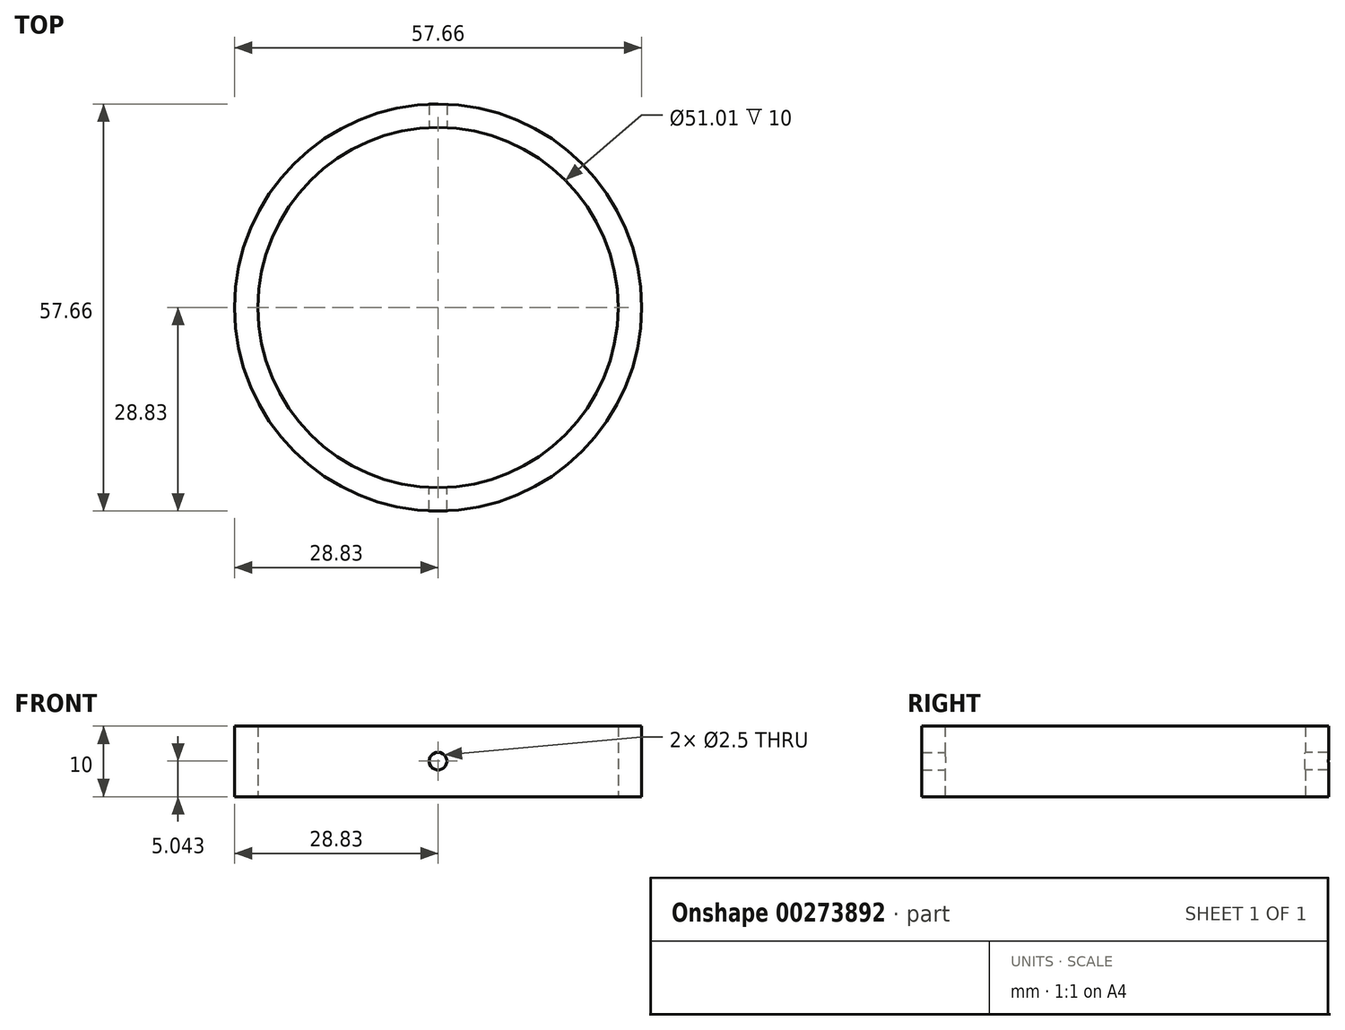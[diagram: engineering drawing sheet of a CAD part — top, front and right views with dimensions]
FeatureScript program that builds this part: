
annotation { "Feature Type Name" : "Feature", "Feature Type Description" : "" }
export const myFeature = defineFeature(function(context is Context, id is Id, definition is map)
    precondition{}
    {
        {
            var Q0;
            Q0=qCreatedBy(makeId("Top.planeOp"),FACE);
            var sketch = newSketch(context, id + "F0", { "sketchPlane" : qUnion([Q0])});
            skCircle(sketch, "E0", {"center": v(0, -0.27) * mm, "radius": 28.67 * mm});
            skSolve(sketch);
        }
        {
            var Q0;
            Q0=qCreatedBy(makeId("Top.planeOp"),FACE);
            cPlane(context, id + "F1", {"entities" : qUnion([Q0]), "cplaneType" : CPlaneType.OFFSET, "offset" : 140 * mm, "width" : 150 * mm, "height" : 150 * mm});
        }
        {
            var Q0;
            Q0=qCreatedBy(id+"F1.planeOp",FACE);
            var sketch = newSketch(context, id + "F2", { "sketchPlane" : qUnion([Q0])});
            skCircle(sketch, "E1", {"center": v(0, 0.28) * mm, "radius": 45.83 * mm});
            skSolve(sketch);
        }
        {
            var Q0;
            Q0=makeQuery(id+"F2.imprint","IMPRINT",FACE,{"disambiguationData":[TD([[makeQuery(id+"F2.imprint","IMPRINT",EDGE,{"derivedFrom":sQuery(id+"F2.wireOp",EDGE,"E1")}),1.0]])]});
            var Q1;
            Q1=makeQuery(id+"F0.imprint","IMPRINT",FACE,{"disambiguationData":[TD([[makeQuery(id+"F0.imprint","IMPRINT",EDGE,{"derivedFrom":sQuery(id+"F0.wireOp",EDGE,"E0")}),1.0]])]});
            loft(context, id + "F3", {"sheetProfilesArray" : [{ "sheetProfileEntities" : qUnion([Q0]) }, { "sheetProfileEntities" : qUnion([Q1]) }]});
        }
        {
            var Q0;
            Q0=makeQuery(id+"F3.opLoft","CAP_FACE",FACE,{"disambiguationData":[OSD([makeQuery(id+"F2.imprint","IMPRINT",FACE,{"disambiguationData":[TD([[makeQuery(id+"F2.imprint","IMPRINT",EDGE,{"derivedFrom":sQuery(id+"F2.wireOp",EDGE,"E1")}),1.0]])]})])],"isStart":true});
            var Q1;
            Q1=makeQuery(id+"F3.opLoft","CAP_FACE",FACE,{"disambiguationData":[OSD([makeQuery(id+"F0.imprint","IMPRINT",FACE,{"disambiguationData":[TD([[makeQuery(id+"F0.imprint","IMPRINT",EDGE,{"derivedFrom":sQuery(id+"F0.wireOp",EDGE,"E0")}),1.0]])]})])],"isStart":true});
            shell(context, id + "F4", {"entities" : qUnion([Q0, Q1]), "thickness" : 2.5 * mm});
        }
        {
            var Q0;
            Q0=makeQuery(id+"F3.opLoft","CAP_FACE",FACE,{"disambiguationData":[OSD([makeQuery(id+"F0.imprint","IMPRINT",FACE,{"disambiguationData":[TD([[makeQuery(id+"F0.imprint","IMPRINT",EDGE,{"derivedFrom":sQuery(id+"F0.wireOp",EDGE,"E0")}),1.0]])]})])],"isStart":true});
            var sketch = newSketch(context, id + "F5", { "sketchPlane" : qUnion([Q0])});
            skCircle(sketch, "E2", {"center": v(0, 0) * mm, "radius": 29.29 * mm});
            skCircle(sketch, "E3", {"center": v(0, 0) * mm, "radius": 33.52 * mm});
            skSolve(sketch);
        }
        {
            var Q0;
            Q0=makeQuery(id+"F5.imprint","IMPRINT",FACE,{"disambiguationData":[TD([[makeQuery(id+"F5.imprint","IMPRINT",EDGE,{"derivedFrom":sQuery(id+"F5.wireOp",EDGE,"E2")}),-1.0]])]});
            extrude(context, id + "F6", {"entities" : qUnion([Q0]), "depth" : 15 * mm});
        }
        {
            var Q0;
            Q0=makeQuery(id+"F3.opLoft","SWEPT_BODY",BODY,{"disambiguationData":[OSD([makeQuery(id+"F0.imprint","IMPRINT",FACE,{"disambiguationData":[TD([[makeQuery(id+"F0.imprint","IMPRINT",EDGE,{"derivedFrom":sQuery(id+"F0.wireOp",EDGE,"E0")}),1.0]])]}),makeQuery(id+"F2.imprint","IMPRINT",FACE,{"disambiguationData":[TD([[makeQuery(id+"F2.imprint","IMPRINT",EDGE,{"derivedFrom":sQuery(id+"F2.wireOp",EDGE,"E1")}),1.0]])]})])]});
            deleteBodies(context, id + "F7", {"entities" : qUnion([Q0])});
        }
        {
            var Q0;
            Q0=qCreatedBy(makeId("Top.planeOp"),FACE);
            cPlane(context, id + "F8", {"entities" : qUnion([Q0]), "cplaneType" : CPlaneType.OFFSET, "offset" : 7.8 * mm, "oppositeDirection" : true, "width" : 150 * mm, "height" : 150 * mm});
        }
        {
            var Q0;
            Q0=qCreatedBy(id+"F8.planeOp",FACE);
            var sketch = newSketch(context, id + "F9", { "sketchPlane" : qUnion([Q0])});
            skCircle(sketch, "E4", {"center": v(0, 0) * mm, "radius": 28.83 * mm});
            skCircle(sketch, "E5", {"center": v(0, 0) * mm, "radius": 25.5 * mm});
            skSolve(sketch);
        }
        {
            var Q0;
            Q0=makeQuery(id+"F9.imprint","IMPRINT",FACE,{"disambiguationData":[TD([[makeQuery(id+"F9.imprint","IMPRINT",EDGE,{"derivedFrom":sQuery(id+"F9.wireOp",EDGE,"E4")}),1.0]])]});
            extrude(context, id + "F10", {"entities" : qUnion([Q0]), "endBound" : BoundingType.SYMMETRIC, "depth" : 10 * mm});
        }
        {
            var Q0;
            Q0=qCreatedBy(makeId("Front.planeOp"),FACE);
            var sketch = newSketch(context, id + "F11", { "sketchPlane" : qUnion([Q0])});
            skCircle(sketch, "E6", {"center": v(0, -7.76) * mm, "radius": 1.25 * mm});
            skSolve(sketch);
        }
        {
            var Q0;
            Q0=makeQuery(id+"F11.imprint","IMPRINT",FACE,{"disambiguationData":[TD([[makeQuery(id+"F11.imprint","IMPRINT",EDGE,{"derivedFrom":sQuery(id+"F11.wireOp",EDGE,"E6")}),1.0]])]});
            extrude(context, id + "F12", {"entities" : qUnion([Q0]), "operationType" : NewBodyOperationType.REMOVE, "endBound" : BoundingType.THROUGH_ALL, "depth" : 25 * mm});
        }
        {
            var Q0;
            Q0=makeQuery(id+"F11.imprint","IMPRINT",FACE,{"disambiguationData":[TD([[makeQuery(id+"F11.imprint","IMPRINT",EDGE,{"derivedFrom":sQuery(id+"F11.wireOp",EDGE,"E6")}),1.0]])]});
            extrude(context, id + "F13", {"entities" : qUnion([Q0]), "operationType" : NewBodyOperationType.REMOVE, "oppositeDirection" : true, "depth" : 31 * mm});
        }
        {
            var Q0;
            Q0=qCreatedBy(makeId("Top.planeOp"),FACE);
            var sketch = newSketch(context, id + "F14", { "sketchPlane" : qUnion([Q0])});
            skCircle(sketch, "E7", {"center": v(0, 0) * mm, "radius": 25.17 * mm});
            skSolve(sketch);
        }
        {
            var Q0;
            Q0=makeQuery(id+"F14.imprint","IMPRINT",FACE,{"disambiguationData":[TD([[makeQuery(id+"F14.imprint","IMPRINT",EDGE,{"derivedFrom":sQuery(id+"F14.wireOp",EDGE,"E7")}),1.0]])]});
            extrude(context, id + "F15", {"entities" : qUnion([Q0]), "endBound" : BoundingType.SYMMETRIC, "depth" : 0.75 * mm});
        }
        {
            var Q0;
            Q0=qCreatedBy(makeId("Right.planeOp"),FACE);
            var sketch = newSketch(context, id + "F16", { "sketchPlane" : qUnion([Q0])});
            skCircle(sketch, "E8", {"center": v(0, 0) * mm, "radius": 1.1 * mm});
            skSolve(sketch);
        }
        {
            var Q0;
            Q0=makeQuery(id+"F16.imprint","IMPRINT",FACE,{"disambiguationData":[TD([[makeQuery(id+"F16.imprint","IMPRINT",EDGE,{"derivedFrom":sQuery(id+"F16.wireOp",EDGE,"E8")}),1.0]])]});
            extrude(context, id + "F17", {"entities" : qUnion([Q0]), "operationType" : NewBodyOperationType.ADD, "depth" : 38 * mm});
        }
        {
            var Q0;
            Q0=makeQuery(id+"F16.imprint","IMPRINT",FACE,{"disambiguationData":[TD([[makeQuery(id+"F16.imprint","IMPRINT",EDGE,{"derivedFrom":sQuery(id+"F16.wireOp",EDGE,"E8")}),1.0]])]});
            extrude(context, id + "F18", {"entities" : qUnion([Q0]), "operationType" : NewBodyOperationType.ADD, "oppositeDirection" : true, "depth" : 31 * mm});
        }
        {
            var Q0;
            Q0=makeQuery(id+"F17.opExtrude","CAP_FACE",FACE,{"disambiguationData":[OSD([sQuery(id+"F16.wireOp",EDGE,"E8")])],"isStart":false});
            var sketch = newSketch(context, id + "F19", { "sketchPlane" : qUnion([Q0])});
            skLineSegment(sketch, "E9.bottom", {"start": v(-1.1, 0) * mm, "end": v(1.1, 0) * mm});
            skLineSegment(sketch, "E9.left", {"start": v(-1.1, 0) * mm, "end": v(-1.1, 2.58) * mm});
            skLineSegment(sketch, "E9.right", {"start": v(1.1, 0) * mm, "end": v(1.1, 2.58) * mm});
            skArc(sketch, "E10", {"start": v(1.1, 2.58) * mm, "mid": v(0, 3.43) * mm, "end": v(-1.1, 2.58) * mm});
            skSolve(sketch);
        }
        {
            var Q0;
            {var subQ1=sQuery(id+"F19.wireOp",EDGE,"E9.left");Q0=makeQuery(id+"F19.imprint","IMPRINT",FACE,{"disambiguationData":[TD([[makeQuery(id+"F19.imprint","IMPRINT",EDGE,{"derivedFrom":subQ1}),-1.0]])]});}
            var Q1;
            {var subQ0=sQuery(id+"F19.wireOp",EDGE,"E9.bottom");var subQ1=makeQuery(id+"F17.opExtrude","CAP_EDGE",EDGE,{"disambiguationData":[OSD([sQuery(id+"F16.wireOp",EDGE,"E8")])],"isStart":false});var subQ3=makeQuery(id+"F19.imprint","INTERSECT",VERTEX,{"derivedFrom":[subQ1,subQ0]});Q1=makeQuery(id+"F19.imprint","IMPRINT",FACE,{"disambiguationData":[TD([[makeQuery(id+"F19.imprint","IMPRINT",EDGE,{"disambiguationData":[TD([[subQ3,1.0]])],"derivedFrom":subQ0}),1.0]])]});}
            extrude(context, id + "F20", {"entities" : qUnion([Q0, Q1]), "operationType" : NewBodyOperationType.ADD, "oppositeDirection" : true, "depth" : 1.25 * mm});
        }
        {
            var Q0;
            Q0=makeQuery(id+"F6.opExtrude","SWEPT_BODY",BODY,{"disambiguationData":[OSD([sQuery(id+"F5.wireOp",EDGE,"E2"),sQuery(id+"F5.wireOp",EDGE,"E3")])]});
            deleteBodies(context, id + "F21", {"entities" : qUnion([Q0])});
        }
    });
